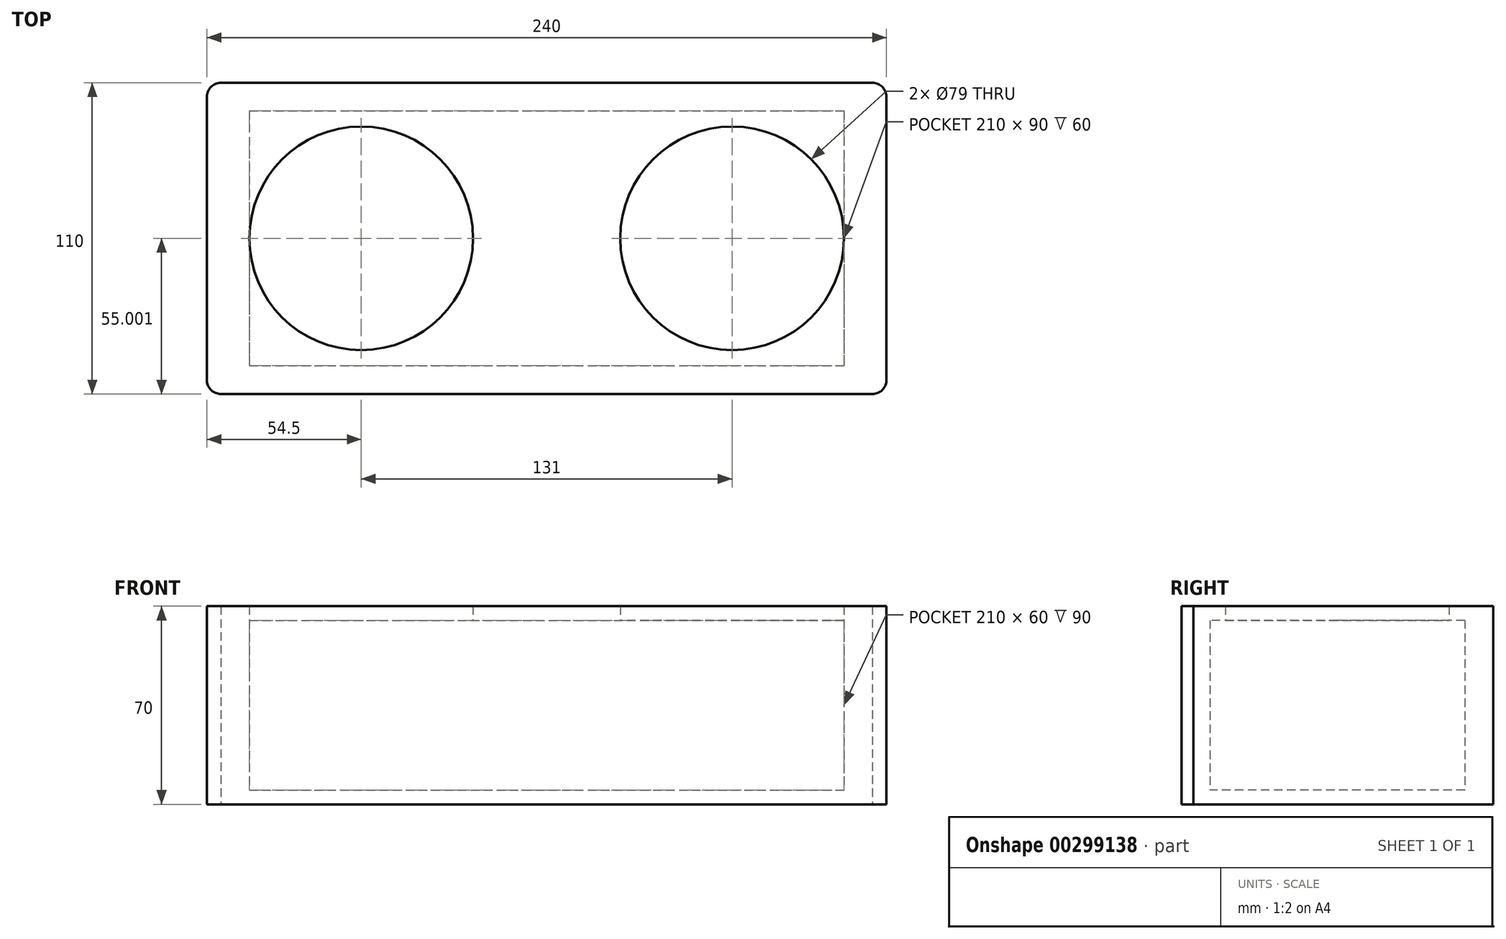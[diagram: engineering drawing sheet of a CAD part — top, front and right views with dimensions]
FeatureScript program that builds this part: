
annotation { "Feature Type Name" : "Feature", "Feature Type Description" : "" }
export const myFeature = defineFeature(function(context is Context, id is Id, definition is map)
    precondition{}
    {
        {
            var Q0;
            Q0=qCreatedBy(makeId("Top.planeOp"),FACE);
            var sketch = newSketch(context, id + "F0", { "sketchPlane" : qUnion([Q0])});
            skLineSegment(sketch, "E0", {"start": v(-104.8, 50.3) * mm, "end": v(125.35, 50.3) * mm});
            skLineSegment(sketch, "E1", {"start": v(130.28, 45.3) * mm, "end": v(130.28, -55.54) * mm});
            skLineSegment(sketch, "E2", {"start": v(125.35, -59.7) * mm, "end": v(-104.8, -59.7) * mm});
            skLineSegment(sketch, "E3", {"start": v(-109.72, -55.54) * mm, "end": v(-109.72, 45.3) * mm});
            skArc(sketch, "E4", {"start": v(-109.72, -55.54) * mm, "mid": v(-108.02, -58.52) * mm, "end": v(-104.8, -59.7) * mm});
            skArc(sketch, "E5", {"start": v(125.35, -59.7) * mm, "mid": v(128.58, -58.52) * mm, "end": v(130.28, -55.54) * mm});
            skArc(sketch, "E6", {"start": v(-104.8, 50.3) * mm, "mid": v(-108.28, 48.81) * mm, "end": v(-109.72, 45.3) * mm});
            skArc(sketch, "E7", {"start": v(130.28, 45.3) * mm, "mid": v(128.84, 48.81) * mm, "end": v(125.35, 50.3) * mm});
            skSolve(sketch);
        }
        {
            var Q0;
            Q0 = qSketchRegion(id + "F0", true);
            extrude(context, id + "F1", {"entities" : qUnion([Q0]), "depth" : 5 * mm});
        }
        {
            var Q0;
            Q0=makeQuery(id+"F1.opExtrude","CAP_FACE",FACE,{"disambiguationData":[OSD([sQuery(id+"F0.wireOp",EDGE,"E0"),sQuery(id+"F0.wireOp",EDGE,"E1"),sQuery(id+"F0.wireOp",EDGE,"E2"),sQuery(id+"F0.wireOp",EDGE,"E3"),sQuery(id+"F0.wireOp",EDGE,"E4"),sQuery(id+"F0.wireOp",EDGE,"E5"),sQuery(id+"F0.wireOp",EDGE,"E6"),sQuery(id+"F0.wireOp",EDGE,"E7")])],"isStart":false});
            var sketch = newSketch(context, id + "F2", { "sketchPlane" : qUnion([Q0])});
            skLineSegment(sketch, "E8", {"start": v(-104.8, 50.3) * mm, "end": v(125.35, 50.3) * mm});
            skLineSegment(sketch, "E9", {"start": v(-109.72, 45.3) * mm, "end": v(-109.72, -55.54) * mm});
            skLineSegment(sketch, "E10", {"start": v(-104.8, -59.7) * mm, "end": v(125.35, -59.7) * mm});
            skLineSegment(sketch, "E11", {"start": v(130.28, 45.3) * mm, "end": v(130.28, -55.54) * mm});
            skArc(sketch, "E12", {"start": v(-104.8, 50.3) * mm, "mid": v(-108.28, 48.81) * mm, "end": v(-109.72, 45.3) * mm});
            skArc(sketch, "E13", {"start": v(130.28, 45.3) * mm, "mid": v(128.84, 48.81) * mm, "end": v(125.35, 50.3) * mm});
            skArc(sketch, "E14", {"start": v(125.35, -59.7) * mm, "mid": v(128.78, -58.76) * mm, "end": v(130.28, -55.54) * mm});
            skArc(sketch, "E15", {"start": v(-109.72, -55.54) * mm, "mid": v(-108.02, -58.52) * mm, "end": v(-104.8, -59.7) * mm});
            skLineSegment(sketch, "E16.bottom", {"start": v(-94.72, 40.3) * mm, "end": v(115.28, 40.3) * mm});
            skLineSegment(sketch, "E16.top", {"start": v(-94.72, -49.7) * mm, "end": v(115.28, -49.7) * mm});
            skLineSegment(sketch, "E16.left", {"start": v(-94.72, 40.3) * mm, "end": v(-94.72, -49.7) * mm});
            skLineSegment(sketch, "E16.right", {"start": v(115.28, 40.3) * mm, "end": v(115.28, -49.7) * mm});
            skSolve(sketch);
        }
        {
            var Q0;
            Q0=makeQuery(id+"F2.imprint","IMPRINT",FACE,{"disambiguationData":[TD([[makeQuery(id+"F2.imprint","IMPRINT",EDGE,{"derivedFrom":sQuery(id+"F2.wireOp",EDGE,"E8")}),-1.0]])]});
            extrude(context, id + "F3", {"entities" : qUnion([Q0]), "operationType" : NewBodyOperationType.ADD, "depth" : 60 * mm});
        }
        {
            var Q0;
            Q0=makeQuery(id+"F3.opExtrude","CAP_FACE",FACE,{"disambiguationData":[OSD([sQuery(id+"F0.wireOp",EDGE,"E5"),sQuery(id+"F2.wireOp",EDGE,"E8"),sQuery(id+"F2.wireOp",EDGE,"E9"),sQuery(id+"F2.wireOp",EDGE,"E10"),sQuery(id+"F2.wireOp",EDGE,"E11"),sQuery(id+"F2.wireOp",EDGE,"E12"),sQuery(id+"F2.wireOp",EDGE,"E13"),sQuery(id+"F2.wireOp",EDGE,"E15"),sQuery(id+"F2.wireOp",EDGE,"E16.bottom"),sQuery(id+"F2.wireOp",EDGE,"E16.top"),sQuery(id+"F2.wireOp",EDGE,"E16.left"),sQuery(id+"F2.wireOp",EDGE,"E16.right")])],"isStart":false});
            var sketch = newSketch(context, id + "F4", { "sketchPlane" : qUnion([Q0])});
            skLineSegment(sketch, "E17", {"start": v(-104.8, 50.3) * mm, "end": v(125.35, 50.3) * mm});
            skLineSegment(sketch, "E18", {"start": v(-109.72, 45.3) * mm, "end": v(-109.72, -55.54) * mm});
            skLineSegment(sketch, "E19", {"start": v(130.28, 45.3) * mm, "end": v(130.28, -55.54) * mm});
            skLineSegment(sketch, "E20", {"start": v(125.35, -59.7) * mm, "end": v(-104.8, -59.7) * mm});
            skArc(sketch, "E21", {"start": v(-109.72, -55.54) * mm, "mid": v(-108.02, -58.52) * mm, "end": v(-104.8, -59.7) * mm});
            skArc(sketch, "E22", {"start": v(-104.8, 50.3) * mm, "mid": v(-108.3, 48.83) * mm, "end": v(-109.72, 45.3) * mm});
            skArc(sketch, "E23", {"start": v(130.28, 45.3) * mm, "mid": v(128.84, 48.81) * mm, "end": v(125.35, 50.3) * mm});
            skArc(sketch, "E24", {"start": v(125.35, -59.7) * mm, "mid": v(128.58, -58.52) * mm, "end": v(130.28, -55.54) * mm});
            skCircle(sketch, "E25", {"center": v(-55.22, -4.7) * mm, "radius": 39.5 * mm});
            skCircle(sketch, "E26", {"center": v(75.78, -4.7) * mm, "radius": 39.5 * mm});
            skSolve(sketch);
        }
        {
            var Q0;
            Q0=makeQuery(id+"F4.imprint","IMPRINT",FACE,{"disambiguationData":[TD([[makeQuery(id+"F4.imprint","IMPRINT",EDGE,{"derivedFrom":sQuery(id+"F4.wireOp",EDGE,"E17")}),-1.0]])]});
            var Q1;
            {var subQ3=sQuery(id+"F4.wireOp",EDGE,"E25");Q1=makeQuery(id+"F4.imprint","IMPRINT",FACE,{"disambiguationData":[TD([[makeQuery(id+"F4.imprint","IMPRINT",EDGE,{"derivedFrom":subQ3}),-1.0]])]});}
            extrude(context, id + "F5", {"entities" : qUnion([Q0, Q1]), "operationType" : NewBodyOperationType.ADD, "depth" : 5 * mm});
        }
    });
